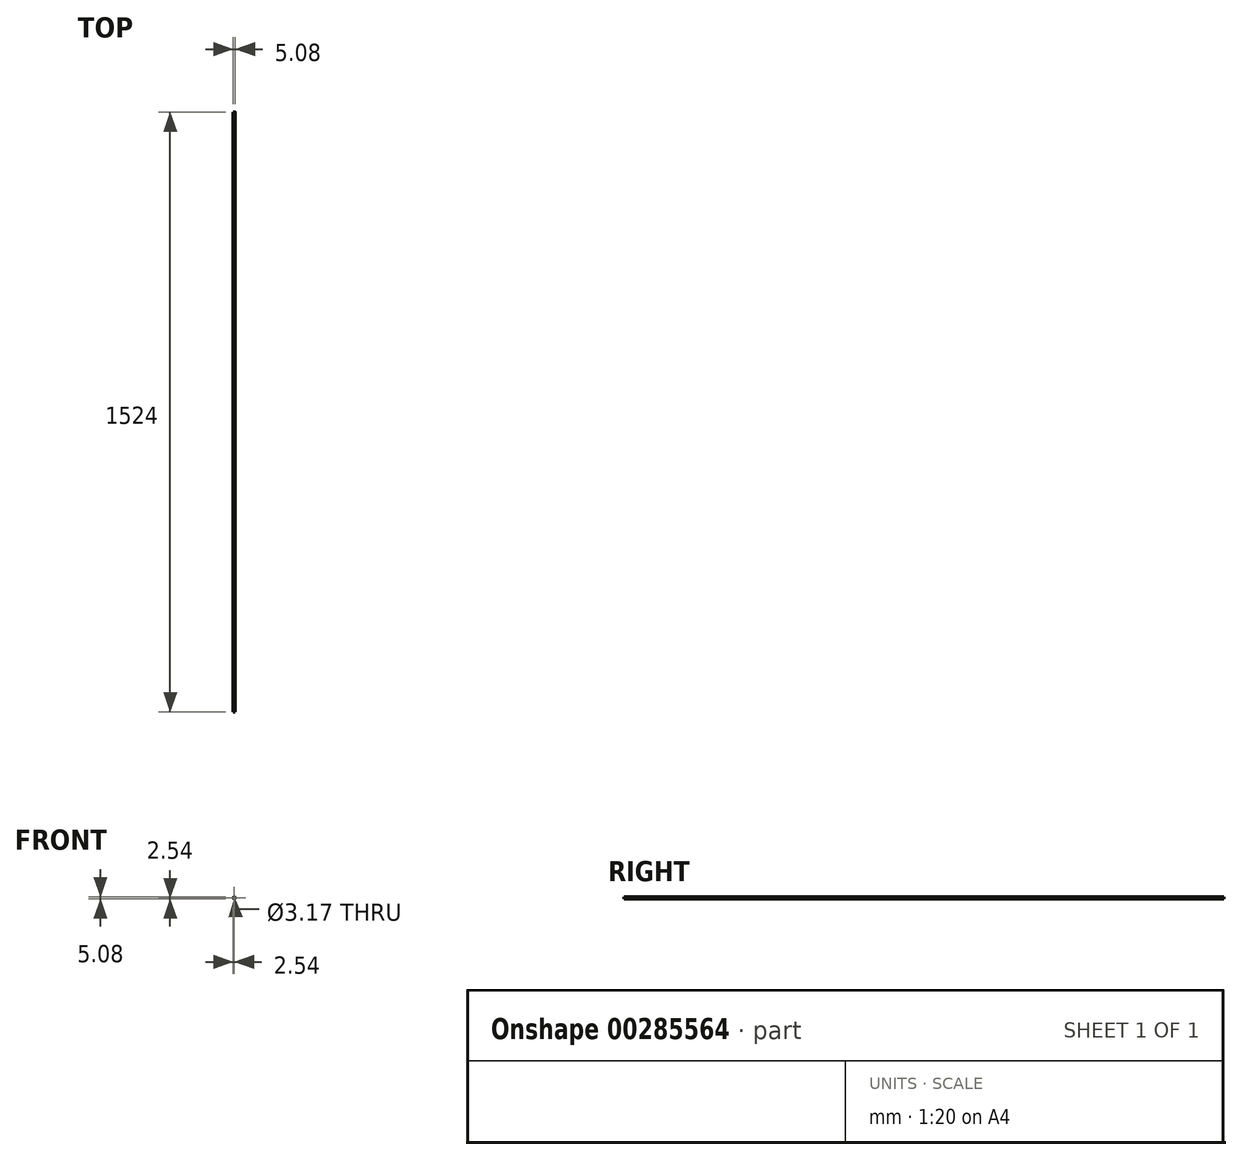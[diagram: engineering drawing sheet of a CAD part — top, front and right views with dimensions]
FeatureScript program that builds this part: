
annotation { "Feature Type Name" : "Feature", "Feature Type Description" : "" }
export const myFeature = defineFeature(function(context is Context, id is Id, definition is map)
    precondition{}
    {
        {
            var Q0;
            Q0=qCreatedBy(makeId("Front.planeOp"),FACE);
            var sketch = newSketch(context, id + "F0", { "sketchPlane" : qUnion([Q0])});
            skCircle(sketch, "E0", {"center": v(0, 0) * mm, "radius": 1.59 * mm});
            skCircle(sketch, "E1", {"center": v(0, 0) * mm, "radius": 2.54 * mm});
            skSolve(sketch);
        }
        {
            var Q0;
            Q0=makeQuery(id+"F0.imprint","IMPRINT",FACE,{"disambiguationData":[TD([[makeQuery(id+"F0.imprint","IMPRINT",EDGE,{"derivedFrom":sQuery(id+"F0.wireOp",EDGE,"E0")}),-1.0]])]});
            extrude(context, id + "F1", {"entities" : qUnion([Q0]), "depth" : 1524 * mm});
        }
    });
